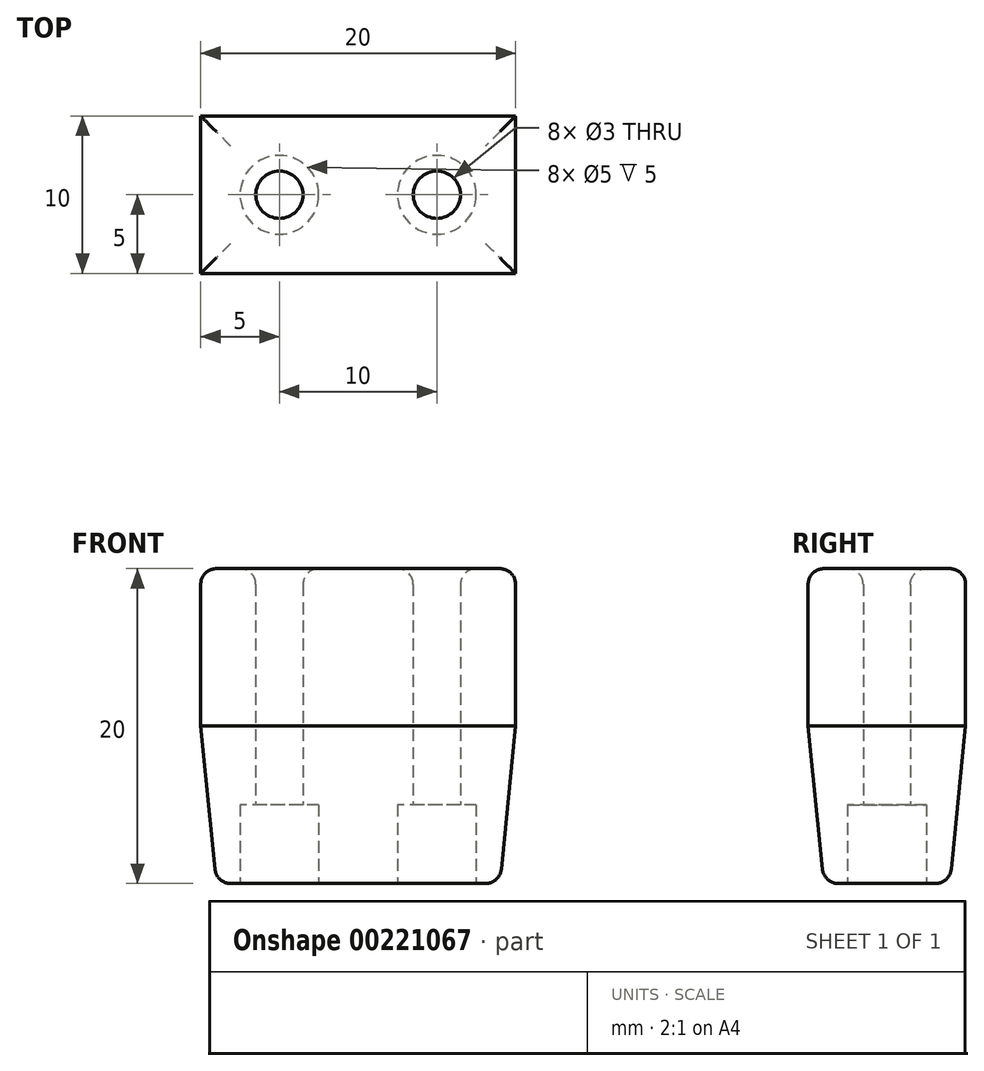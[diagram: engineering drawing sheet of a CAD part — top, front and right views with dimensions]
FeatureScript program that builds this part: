
annotation { "Feature Type Name" : "Feature", "Feature Type Description" : "" }
export const myFeature = defineFeature(function(context is Context, id is Id, definition is map)
    precondition{}
    {
        {
            var Q0;
            Q0=qCreatedBy(makeId("Top.planeOp"),FACE);
            var sketch = newSketch(context, id + "F0", { "sketchPlane" : qUnion([Q0])});
            skLineSegment(sketch, "E0.bottom", {"start": v(-10, 5) * mm, "end": v(10, 5) * mm});
            skLineSegment(sketch, "E0.top", {"start": v(-10, -5) * mm, "end": v(10, -5) * mm});
            skLineSegment(sketch, "E0.left", {"start": v(-10, 5) * mm, "end": v(-10, -5) * mm});
            skLineSegment(sketch, "E0.right", {"start": v(10, 5) * mm, "end": v(10, -5) * mm});
            skLineSegment(sketch, "E1.bottom", {"start": v(-8.85, 3.75) * mm, "end": v(8.85, 3.75) * mm});
            skLineSegment(sketch, "E1.top", {"start": v(-8.85, -3.75) * mm, "end": v(8.85, -3.75) * mm});
            skLineSegment(sketch, "E1.left", {"start": v(-8.85, 3.75) * mm, "end": v(-8.85, -3.75) * mm});
            skLineSegment(sketch, "E1.right", {"start": v(8.85, 3.75) * mm, "end": v(8.85, -3.75) * mm});
            skCircle(sketch, "E2", {"center": v(-5, 0) * mm, "radius": 2.5 * mm});
            skCircle(sketch, "E3", {"center": v(5, 0) * mm, "radius": 2.5 * mm});
            skCircle(sketch, "E4", {"center": v(-5, 0) * mm, "radius": 1.5 * mm});
            skCircle(sketch, "E5", {"center": v(5, 0) * mm, "radius": 1.5 * mm});
            skSolve(sketch);
        }
        {
            var Q0;
            Q0=makeQuery(id+"F0.imprint","IMPRINT",FACE,{"disambiguationData":[TD([[makeQuery(id+"F0.imprint","IMPRINT",EDGE,{"derivedFrom":sQuery(id+"F0.wireOp",EDGE,"E1.bottom")}),-1.0]])]});
            var Q1;
            Q1=makeQuery(id+"F0.imprint","IMPRINT",FACE,{"disambiguationData":[TD([[makeQuery(id+"F0.imprint","IMPRINT",EDGE,{"derivedFrom":sQuery(id+"F0.wireOp",EDGE,"E0.bottom")}),-1.0]])]});
            var Q2;
            Q2=makeQuery(id+"F0.imprint","IMPRINT",FACE,{"disambiguationData":[TD([[makeQuery(id+"F0.imprint","IMPRINT",EDGE,{"derivedFrom":sQuery(id+"F0.wireOp",EDGE,"E3")}),1.0]])]});
            var Q3;
            Q3=makeQuery(id+"F0.imprint","IMPRINT",FACE,{"disambiguationData":[TD([[makeQuery(id+"F0.imprint","IMPRINT",EDGE,{"derivedFrom":sQuery(id+"F0.wireOp",EDGE,"E2")}),1.0]])]});
            extrude(context, id + "F1", {"entities" : qUnion([Q0, Q1, Q2, Q3]), "depth" : 20 * mm});
        }
        {
            var Q0;
            Q0=makeQuery(id+"F0.imprint","IMPRINT",FACE,{"disambiguationData":[TD([[makeQuery(id+"F0.imprint","IMPRINT",EDGE,{"derivedFrom":sQuery(id+"F0.wireOp",EDGE,"E2")}),1.0]])]});
            var Q1;
            Q1=makeQuery(id+"F0.imprint","IMPRINT",FACE,{"disambiguationData":[TD([[makeQuery(id+"F0.imprint","IMPRINT",EDGE,{"derivedFrom":sQuery(id+"F0.wireOp",EDGE,"E3")}),1.0]])]});
            extrude(context, id + "F2", {"entities" : qUnion([Q0, Q1]), "operationType" : NewBodyOperationType.REMOVE, "depth" : 5 * mm});
        }
        {
            var Q0;
            Q0=makeQuery(id+"F1.opExtrude","CAP_EDGE",EDGE,{"disambiguationData":[OSD([sQuery(id+"F0.wireOp",EDGE,"E0.top")])],"isStart":true});
            var Q1;
            Q1=makeQuery(id+"F1.opExtrude","CAP_EDGE",EDGE,{"disambiguationData":[OSD([sQuery(id+"F0.wireOp",EDGE,"E0.left")])],"isStart":true});
            var Q2;
            Q2=makeQuery(id+"F1.opExtrude","CAP_EDGE",EDGE,{"disambiguationData":[OSD([sQuery(id+"F0.wireOp",EDGE,"E0.bottom")])],"isStart":true});
            var Q3;
            Q3=makeQuery(id+"F1.opExtrude","CAP_EDGE",EDGE,{"disambiguationData":[OSD([sQuery(id+"F0.wireOp",EDGE,"E0.right")])],"isStart":true});
            chamfer(context, id + "F3", {"entities" : qUnion([Q0, Q1, Q2, Q3]), "chamferType" : ChamferType.TWO_OFFSETS, "width1" : 10 * mm, "oppositeDirection" : false, "width2" : 1 * mm, "tangentPropagation" : true});
        }
        {
            var Q0;
            {var subQ0=sQuery(id+"F0.wireOp",EDGE,"E0.top");Q0=makeQuery(id+"F3.opChamfer","BLEND_EDGE",EDGE,{"blendedFrom":[makeQuery(id+"F1.opExtrude","CAP_EDGE",EDGE,{"disambiguationData":[OSD([subQ0])],"isStart":true}),makeQuery(id+"F1.opExtrude","CAP_FACE",FACE,{"disambiguationData":[OSD([sQuery(id+"F0.wireOp",EDGE,"E0.bottom"),subQ0,sQuery(id+"F0.wireOp",EDGE,"E0.left"),sQuery(id+"F0.wireOp",EDGE,"E0.right"),sQuery(id+"F0.wireOp",EDGE,"E4"),sQuery(id+"F0.wireOp",EDGE,"E5")])],"isStart":true})],"blendedInto":[makeQuery(id+"F1.opExtrude","CAP_FACE",FACE,{"disambiguationData":[OSD([sQuery(id+"F0.wireOp",EDGE,"E0.bottom"),subQ0,sQuery(id+"F0.wireOp",EDGE,"E0.left"),sQuery(id+"F0.wireOp",EDGE,"E0.right"),sQuery(id+"F0.wireOp",EDGE,"E4"),sQuery(id+"F0.wireOp",EDGE,"E5")])],"isStart":true})]});}
            var Q1;
            {var subQ0=sQuery(id+"F0.wireOp",EDGE,"E0.left");Q1=makeQuery(id+"F3.opChamfer","BLEND_EDGE",EDGE,{"blendedFrom":[makeQuery(id+"F1.opExtrude","CAP_EDGE",EDGE,{"disambiguationData":[OSD([subQ0])],"isStart":true}),makeQuery(id+"F1.opExtrude","CAP_FACE",FACE,{"disambiguationData":[OSD([sQuery(id+"F0.wireOp",EDGE,"E0.bottom"),sQuery(id+"F0.wireOp",EDGE,"E0.top"),subQ0,sQuery(id+"F0.wireOp",EDGE,"E0.right"),sQuery(id+"F0.wireOp",EDGE,"E4"),sQuery(id+"F0.wireOp",EDGE,"E5")])],"isStart":true})],"blendedInto":[makeQuery(id+"F1.opExtrude","CAP_FACE",FACE,{"disambiguationData":[OSD([sQuery(id+"F0.wireOp",EDGE,"E0.bottom"),sQuery(id+"F0.wireOp",EDGE,"E0.top"),subQ0,sQuery(id+"F0.wireOp",EDGE,"E0.right"),sQuery(id+"F0.wireOp",EDGE,"E4"),sQuery(id+"F0.wireOp",EDGE,"E5")])],"isStart":true})]});}
            var Q2;
            {var subQ0=sQuery(id+"F0.wireOp",EDGE,"E0.bottom");Q2=makeQuery(id+"F3.opChamfer","BLEND_EDGE",EDGE,{"blendedFrom":[makeQuery(id+"F1.opExtrude","CAP_EDGE",EDGE,{"disambiguationData":[OSD([subQ0])],"isStart":true}),makeQuery(id+"F1.opExtrude","CAP_FACE",FACE,{"disambiguationData":[OSD([subQ0,sQuery(id+"F0.wireOp",EDGE,"E0.top"),sQuery(id+"F0.wireOp",EDGE,"E0.left"),sQuery(id+"F0.wireOp",EDGE,"E0.right"),sQuery(id+"F0.wireOp",EDGE,"E4"),sQuery(id+"F0.wireOp",EDGE,"E5")])],"isStart":true})],"blendedInto":[makeQuery(id+"F1.opExtrude","CAP_FACE",FACE,{"disambiguationData":[OSD([subQ0,sQuery(id+"F0.wireOp",EDGE,"E0.top"),sQuery(id+"F0.wireOp",EDGE,"E0.left"),sQuery(id+"F0.wireOp",EDGE,"E0.right"),sQuery(id+"F0.wireOp",EDGE,"E4"),sQuery(id+"F0.wireOp",EDGE,"E5")])],"isStart":true})]});}
            var Q3;
            {var subQ0=sQuery(id+"F0.wireOp",EDGE,"E0.right");Q3=makeQuery(id+"F3.opChamfer","BLEND_EDGE",EDGE,{"blendedFrom":[makeQuery(id+"F1.opExtrude","CAP_EDGE",EDGE,{"disambiguationData":[OSD([subQ0])],"isStart":true}),makeQuery(id+"F1.opExtrude","CAP_FACE",FACE,{"disambiguationData":[OSD([sQuery(id+"F0.wireOp",EDGE,"E0.bottom"),sQuery(id+"F0.wireOp",EDGE,"E0.top"),sQuery(id+"F0.wireOp",EDGE,"E0.left"),subQ0,sQuery(id+"F0.wireOp",EDGE,"E4"),sQuery(id+"F0.wireOp",EDGE,"E5")])],"isStart":true})],"blendedInto":[makeQuery(id+"F1.opExtrude","CAP_FACE",FACE,{"disambiguationData":[OSD([sQuery(id+"F0.wireOp",EDGE,"E0.bottom"),sQuery(id+"F0.wireOp",EDGE,"E0.top"),sQuery(id+"F0.wireOp",EDGE,"E0.left"),subQ0,sQuery(id+"F0.wireOp",EDGE,"E4"),sQuery(id+"F0.wireOp",EDGE,"E5")])],"isStart":true})]});}
            var Q4;
            Q4=makeQuery(id+"F1.opExtrude","CAP_EDGE",EDGE,{"disambiguationData":[OSD([sQuery(id+"F0.wireOp",EDGE,"E0.top")])],"isStart":false});
            var Q5;
            Q5=makeQuery(id+"F1.opExtrude","CAP_EDGE",EDGE,{"disambiguationData":[OSD([sQuery(id+"F0.wireOp",EDGE,"E0.right")])],"isStart":false});
            var Q6;
            Q6=makeQuery(id+"F1.opExtrude","CAP_FACE",FACE,{"disambiguationData":[OSD([sQuery(id+"F0.wireOp",EDGE,"E0.bottom"),sQuery(id+"F0.wireOp",EDGE,"E0.top"),sQuery(id+"F0.wireOp",EDGE,"E0.left"),sQuery(id+"F0.wireOp",EDGE,"E0.right"),sQuery(id+"F0.wireOp",EDGE,"E4"),sQuery(id+"F0.wireOp",EDGE,"E5")])],"isStart":false});
            var Q7;
            Q7=makeQuery(id+"F2.boolean.opBoolean","COPY",EDGE,{"derivedFrom":makeQuery(id+"F2.opExtrude","CAP_EDGE",EDGE,{"disambiguationData":[OSD([sQuery(id+"F0.wireOp",EDGE,"E3")])],"isStart":true})});
            var Q8;
            Q8=makeQuery(id+"F2.boolean.opBoolean","COPY",EDGE,{"derivedFrom":makeQuery(id+"F2.opExtrude","CAP_EDGE",EDGE,{"disambiguationData":[OSD([sQuery(id+"F0.wireOp",EDGE,"E2")])],"isStart":true})});
            fillet(context, id + "F4", {"entities" : qUnion([Q0, Q1, Q2, Q3, Q4, Q5, Q6, Q7, Q8]), "radius" : 1 * mm, "tangentPropagation" : true, "allowEdgeOverflow" : false});
        }
    });
